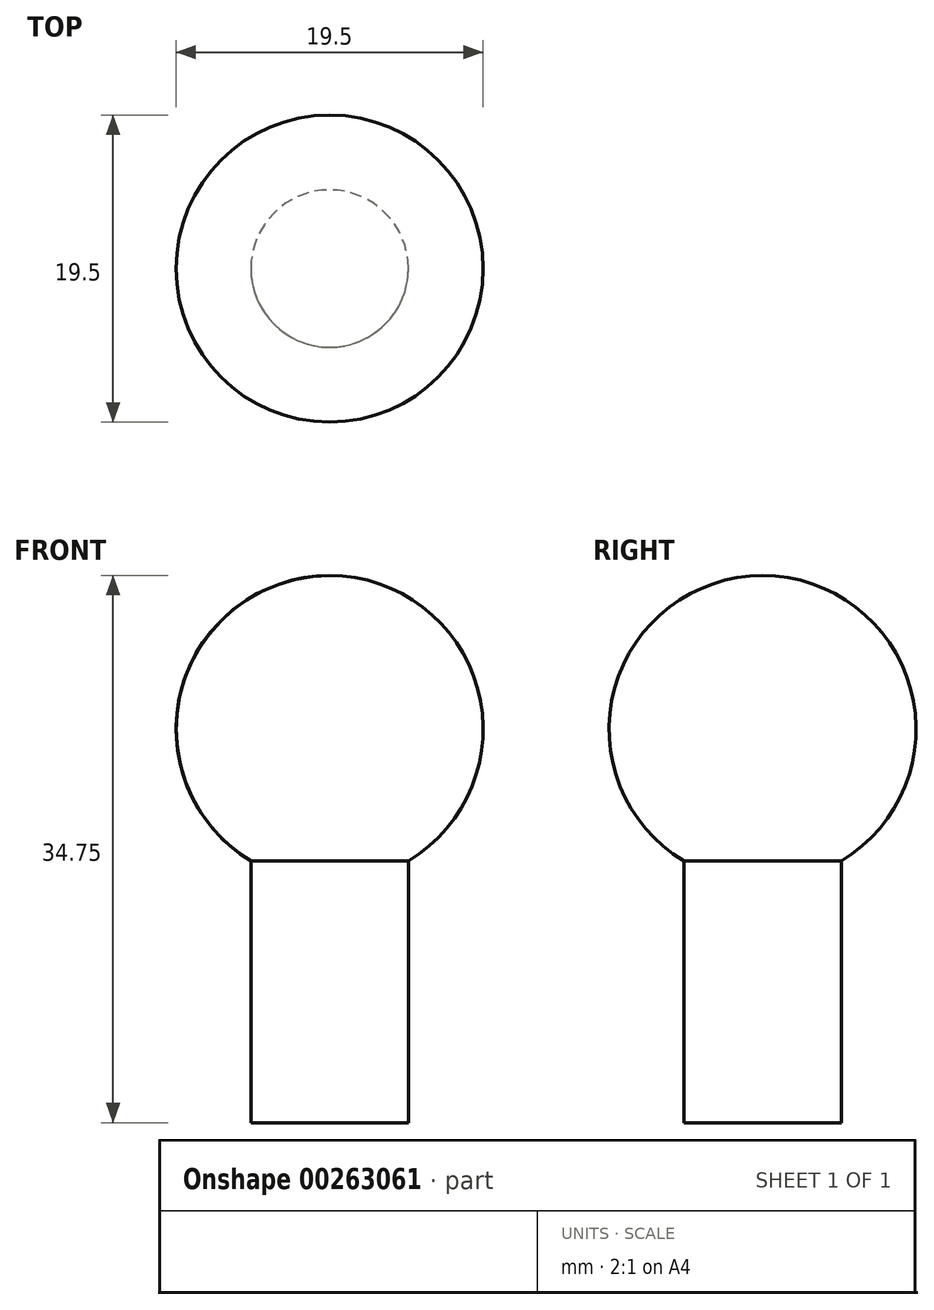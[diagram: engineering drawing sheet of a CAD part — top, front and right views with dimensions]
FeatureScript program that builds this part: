
annotation { "Feature Type Name" : "Feature", "Feature Type Description" : "" }
export const myFeature = defineFeature(function(context is Context, id is Id, definition is map)
    precondition{}
    {
        {
            var Q0;
            Q0=qCreatedBy(makeId("Front.planeOp"),FACE);
            var sketch = newSketch(context, id + "F0", { "sketchPlane" : qUnion([Q0])});
            skArc(sketch, "E0", {"start": v(0, -9.75) * mm, "mid": v(9.75, 0) * mm, "end": v(0, 9.75) * mm});
            skLineSegment(sketch, "E1", {"start": v(0, 9.75) * mm, "end": v(0, -9.75) * mm});
            skSolve(sketch);
        }
        {
            var Q0;
            Q0=makeQuery(id+"F0.imprint","IMPRINT",FACE,{"disambiguationData":[TD([[makeQuery(id+"F0.imprint","IMPRINT",EDGE,{"derivedFrom":sQuery(id+"F0.wireOp",EDGE,"E0")}),1.0]])]});
            var Q1;
            Q1=sQuery(id+"F0.wireOp",EDGE,"E0");
            var Q2;
            Q2=sQuery(id+"F0.wireOp",EDGE,"E1");
            revolve(context, id + "F1", {"entities" : qUnion([Q0]), "surfaceEntities" : qUnion([Q1]), "axis" : qUnion([Q2]), "revolveType" : RevolveType.FULL});
        }
        {
            var Q0;
            Q0=qCreatedBy(makeId("Top.planeOp"),FACE);
            var sketch = newSketch(context, id + "F2", { "sketchPlane" : qUnion([Q0])});
            skCircle(sketch, "E2", {"center": v(0, 0) * mm, "radius": 5 * mm});
            skSolve(sketch);
        }
        {
            var Q0;
            Q0 = qSketchRegion(id + "F2", true);
            extrude(context, id + "F3", {"entities" : qUnion([Q0]), "operationType" : NewBodyOperationType.ADD, "oppositeDirection" : true, "depth" : 25 * mm});
        }
    });
